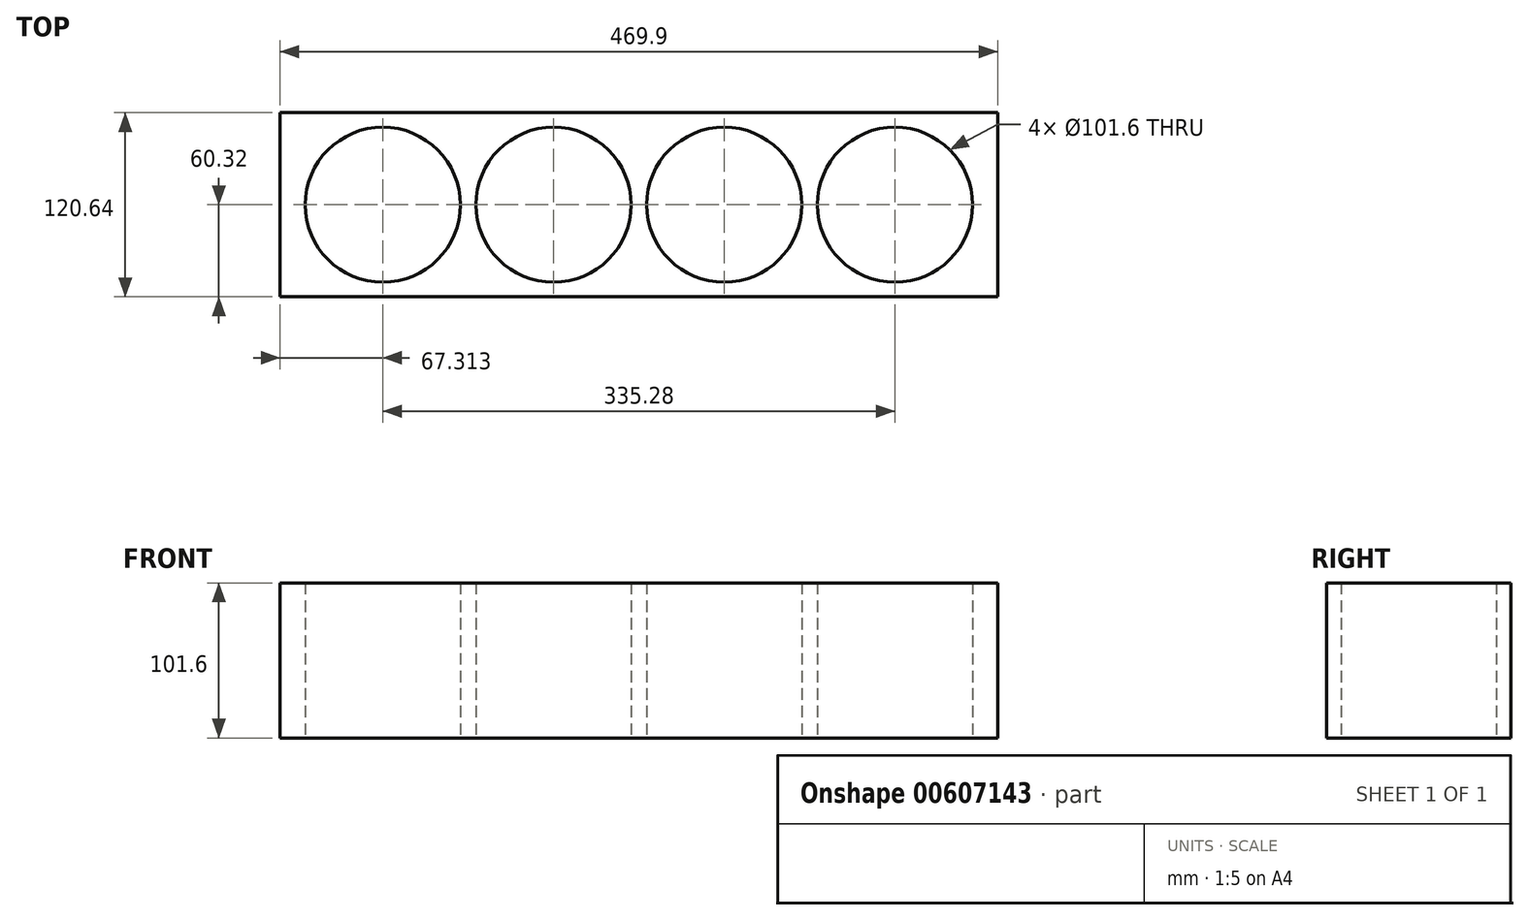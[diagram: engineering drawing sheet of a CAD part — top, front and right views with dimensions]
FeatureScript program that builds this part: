
annotation { "Feature Type Name" : "Feature", "Feature Type Description" : "" }
export const myFeature = defineFeature(function(context is Context, id is Id, definition is map)
    precondition{}
    {
        {
            var Q0;
            Q0=qCreatedBy(makeId("Top.planeOp"),FACE);
            var sketch = newSketch(context, id + "F0", { "sketchPlane" : qUnion([Q0])});
            skCircle(sketch, "E0", {"center": v(-251.32, 0) * mm, "radius": 50.8 * mm});
            skCircle(sketch, "E1.1.0.0", {"center": v(-139.56, 0) * mm, "radius": 50.8 * mm});
            skCircle(sketch, "E1.2.0.0", {"center": v(-27.8, 0) * mm, "radius": 50.8 * mm});
            skCircle(sketch, "E1.3.0.0", {"center": v(83.96, 0) * mm, "radius": 50.8 * mm});
            skLineSegment(sketch, "E1.direction1", {"start": v(-251.32, 0) * mm, "end": v(-139.56, 0) * mm, "construction": true});
            skLineSegment(sketch, "E2", {"start": v(-251.32, 0) * mm, "end": v(83.96, 0) * mm, "construction": true});
            skLineSegment(sketch, "E3.bottom", {"start": v(151.27, 60.32) * mm, "end": v(-318.63, 60.33) * mm});
            skLineSegment(sketch, "E3.top", {"start": v(151.27, -60.33) * mm, "end": v(-318.63, -60.32) * mm});
            skLineSegment(sketch, "E3.left", {"start": v(151.27, 60.32) * mm, "end": v(151.27, -60.33) * mm});
            skLineSegment(sketch, "E3.right", {"start": v(-318.63, 60.33) * mm, "end": v(-318.63, -60.32) * mm});
            skPoint(sketch, "E3.middle", {"position": v(-83.68, 0) * mm});
            skSolve(sketch);
        }
        {
            var Q0;
            Q0=makeQuery(id+"F0.imprint","IMPRINT",FACE,{"disambiguationData":[TD([[makeQuery(id+"F0.imprint","IMPRINT",EDGE,{"derivedFrom":sQuery(id+"F0.wireOp",EDGE,"E0")}),-1.0]])]});
            extrude(context, id + "F1", {"entities" : qUnion([Q0]), "depth" : 101.6 * mm, "offsetDistance" : 25.4 * mm});
        }
    });
